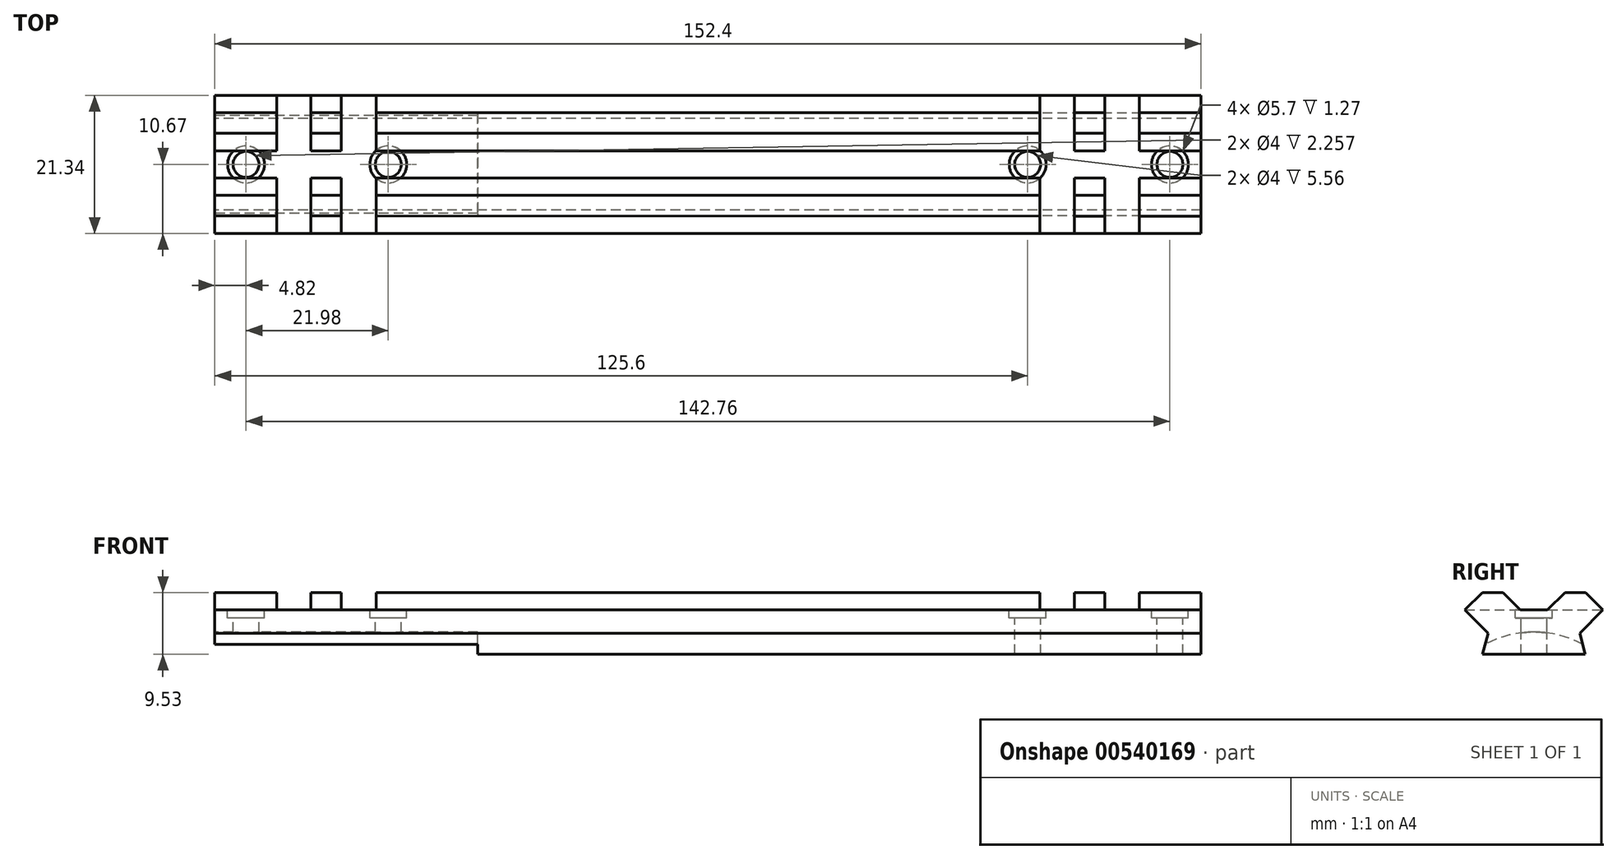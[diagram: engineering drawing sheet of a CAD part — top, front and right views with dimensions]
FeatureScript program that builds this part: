
annotation { "Feature Type Name" : "Feature", "Feature Type Description" : "" }
export const myFeature = defineFeature(function(context is Context, id is Id, definition is map)
    precondition{}
    {
        {
            var Q0;
            Q0=qCreatedBy(makeId("Front.planeOp"),FACE);
            var sketch = newSketch(context, id + "F0", { "sketchPlane" : qUnion([Q0])});
            skLineSegment(sketch, "E0", {"start": v(-76.2, 0) * mm, "end": v(76.2, 0) * mm});
            skLineSegment(sketch, "E1.0", {"start": v(-76.2, 9.53) * mm, "end": v(76.2, 9.52) * mm});
            skLineSegment(sketch, "E2", {"start": v(-76.2, 0) * mm, "end": v(-76.2, 9.53) * mm});
            skLineSegment(sketch, "E3", {"start": v(76.2, 0) * mm, "end": v(76.2, 9.52) * mm});
            skSolve(sketch);
        }
        {
            var Q0;
            Q0=makeQuery(id+"F0.imprint","IMPRINT",FACE,{"disambiguationData":[TD([[makeQuery(id+"F0.imprint","IMPRINT",EDGE,{"derivedFrom":sQuery(id+"F0.wireOp",EDGE,"E0")}),1.0]])]});
            extrude(context, id + "F1", {"entities" : qUnion([Q0]), "endBound" : BoundingType.SYMMETRIC, "depth" : 21.34 * mm, "offsetDistance" : 25.4 * mm});
        }
        {
            var Q0;
            Q0=makeQuery(id+"F1.opExtrude","SWEPT_FACE",FACE,{"disambiguationData":[OSD([sQuery(id+"F0.wireOp",EDGE,"E2")])]});
            var sketch = newSketch(context, id + "F2", { "sketchPlane" : qUnion([Q0])});
            skLineSegment(sketch, "E4", {"start": v(-10.67, 6.83) * mm, "end": v(-7.97, 9.53) * mm});
            skLineSegment(sketch, "E5", {"start": v(-10.67, 6.83) * mm, "end": v(-7.08, 3.24) * mm});
            skLineSegment(sketch, "E6", {"start": v(0, 0) * mm, "end": v(-7.94, 0) * mm});
            skLineSegment(sketch, "E7", {"start": v(-7.94, 0) * mm, "end": v(-7.08, 3.24) * mm});
            skLineSegment(sketch, "E8", {"start": v(0, 6.83) * mm, "end": v(-2.1, 6.83) * mm});
            skLineSegment(sketch, "E9", {"start": v(-2.1, 6.83) * mm, "end": v(-4.8, 9.53) * mm});
            skLineSegment(sketch, "E10", {"start": v(-4.8, 9.53) * mm, "end": v(-7.97, 9.53) * mm});
            skLineSegment(sketch, "E11.MirrorCS", {"start": v(0, 6.83) * mm, "end": v(2.1, 6.83) * mm});
            skLineSegment(sketch, "E12.MirrorCS", {"start": v(2.1, 6.83) * mm, "end": v(4.8, 9.53) * mm});
            skLineSegment(sketch, "E13.MirrorCS", {"start": v(4.8, 9.53) * mm, "end": v(7.97, 9.53) * mm});
            skLineSegment(sketch, "E14.MirrorCS", {"start": v(10.67, 6.83) * mm, "end": v(7.97, 9.53) * mm});
            skLineSegment(sketch, "E15.MirrorCS", {"start": v(10.67, 6.83) * mm, "end": v(7.08, 3.24) * mm});
            skLineSegment(sketch, "E16.MirrorCS", {"start": v(7.94, 0) * mm, "end": v(7.08, 3.24) * mm});
            skLineSegment(sketch, "E17.MirrorCS", {"start": v(0, 0) * mm, "end": v(7.94, 0) * mm});
            skSolve(sketch);
        }
        {
            var Q0;
            {var subQ0=sQuery(id+"F2.wireOp",EDGE,"E5");Q0=makeQuery(id+"F2.imprint","IMPRINT",FACE,{"disambiguationData":[TD([[makeQuery(id+"F2.imprint","IMPRINT",EDGE,{"derivedFrom":subQ0}),-1.0]])]});}
            var Q1;
            {var subQ0=sQuery(id+"F2.wireOp",EDGE,"E4");Q1=makeQuery(id+"F2.imprint","IMPRINT",FACE,{"disambiguationData":[TD([[makeQuery(id+"F2.imprint","IMPRINT",EDGE,{"derivedFrom":subQ0}),1.0]])]});}
            var Q2;
            Q2=makeQuery(id+"F2.imprint","IMPRINT",FACE,{"disambiguationData":[TD([[makeQuery(id+"F2.imprint","IMPRINT",EDGE,{"derivedFrom":sQuery(id+"F2.wireOp",EDGE,"E8")}),-1.0]])]});
            var Q3;
            {var subQ0=sQuery(id+"F2.wireOp",EDGE,"E14.MirrorCS");Q3=makeQuery(id+"F2.imprint","IMPRINT",FACE,{"disambiguationData":[TD([[makeQuery(id+"F2.imprint","IMPRINT",EDGE,{"derivedFrom":subQ0}),-1.0]])]});}
            var Q4;
            {var subQ0=sQuery(id+"F2.wireOp",EDGE,"E15.MirrorCS");Q4=makeQuery(id+"F2.imprint","IMPRINT",FACE,{"disambiguationData":[TD([[makeQuery(id+"F2.imprint","IMPRINT",EDGE,{"derivedFrom":subQ0}),1.0]])]});}
            extrude(context, id + "F3", {"entities" : qUnion([Q0, Q1, Q2, Q3, Q4]), "operationType" : NewBodyOperationType.REMOVE, "oppositeDirection" : true, "depth" : 152.4 * mm, "offsetDistance" : 25.4 * mm});
        }
        {
            var Q0;
            Q0=makeQuery(id+"F1.opExtrude","SWEPT_FACE",FACE,{"disambiguationData":[OSD([sQuery(id+"F0.wireOp",EDGE,"E2")])]});
            var sketch = newSketch(context, id + "F4", { "sketchPlane" : qUnion([Q0])});
            skCircle(sketch, "E18", {"center": v(0, -12.45) * mm, "radius": 15.88 * mm});
            skLineSegment(sketch, "E19", {"start": v(-9.85, 0) * mm, "end": v(9.85, 0) * mm});
            skSolve(sketch);
        }
        {
            var Q0;
            {var subQ0=sQuery(id+"F4.wireOp",EDGE,"E18");var subQ1=makeQuery(id+"F3.boolean.opBoolean","COPY",EDGE,{"derivedFrom":makeQuery(id+"F3.opExtrude","CAP_EDGE",EDGE,{"disambiguationData":[OSD([sQuery(id+"F2.wireOp",EDGE,"E16.MirrorCS")])],"isStart":true})});var subQ2=makeQuery(id+"F4.imprint","INTERSECT",VERTEX,{"derivedFrom":[subQ1,subQ0]});Q0=makeQuery(id+"F4.imprint","IMPRINT",FACE,{"disambiguationData":[TD([[makeQuery(id+"F4.imprint","IMPRINT",EDGE,{"disambiguationData":[TD([[subQ2,-1.0]])],"derivedFrom":subQ0}),1.0]])]});}
            extrude(context, id + "F5", {"entities" : qUnion([Q0]), "operationType" : NewBodyOperationType.REMOVE, "oppositeDirection" : true, "depth" : 40.64 * mm, "offsetDistance" : 25.4 * mm});
        }
        {
            var Q0;
            Q0=makeQuery(id+"F3.boolean.opBoolean","COPY",FACE,{"derivedFrom":makeQuery(id+"F3.opExtrude","SWEPT_FACE",FACE,{"disambiguationData":[OSD([sQuery(id+"F2.wireOp",EDGE,"E8"),sQuery(id+"F2.wireOp",EDGE,"E11.MirrorCS")])]})});
            var sketch = newSketch(context, id + "F6", { "sketchPlane" : qUnion([Q0])});
            skLineSegment(sketch, "E20", {"start": v(-66.67, -10.86) * mm, "end": v(-66.67, 11.03) * mm});
            skPoint(sketch, "E21.orphan", {"position": v(-66.67, 0) * mm});
            skLineSegment(sketch, "E22.0", {"start": v(-61.34, -10.86) * mm, "end": v(-61.34, 11.03) * mm});
            skLineSegment(sketch, "E23.0", {"start": v(-56.64, -10.86) * mm, "end": v(-56.64, 11.03) * mm});
            skLineSegment(sketch, "E24.0", {"start": v(-51.3, -10.86) * mm, "end": v(-51.3, 11.03) * mm});
            skLineSegment(sketch, "E25", {"start": v(-66.67, 11.03) * mm, "end": v(-61.34, 11.03) * mm});
            skLineSegment(sketch, "E26", {"start": v(-66.67, -10.86) * mm, "end": v(-61.34, -10.86) * mm});
            skCircle(sketch, "E27", {"center": v(-71.38, 0) * mm, "radius": 2.86 * mm});
            skCircle(sketch, "E28", {"center": v(-49.4, 0) * mm, "radius": 2.86 * mm});
            skCircle(sketch, "E29.MirrorC", {"center": v(49.4, 0) * mm, "radius": 2.86 * mm});
            skCircle(sketch, "E30.MirrorC", {"center": v(71.38, 0) * mm, "radius": 2.86 * mm});
            skLineSegment(sketch, "E31.MirrorCS", {"start": v(66.67, -10.86) * mm, "end": v(66.67, 11.03) * mm});
            skLineSegment(sketch, "E32.MirrorCS", {"start": v(61.34, -10.86) * mm, "end": v(61.34, 11.03) * mm});
            skLineSegment(sketch, "E33.MirrorCS", {"start": v(56.64, -10.86) * mm, "end": v(56.64, 11.03) * mm});
            skLineSegment(sketch, "E34.MirrorCS", {"start": v(51.3, -10.86) * mm, "end": v(51.3, 11.03) * mm});
            skLineSegment(sketch, "E35.MirrorCS", {"start": v(66.67, 11.03) * mm, "end": v(61.34, 11.03) * mm});
            skLineSegment(sketch, "E36.MirrorCS", {"start": v(66.67, -10.86) * mm, "end": v(61.34, -10.86) * mm});
            skLineSegment(sketch, "E37.trimOffspring", {"start": v(-56.64, 11.03) * mm, "end": v(-51.3, 11.03) * mm});
            skLineSegment(sketch, "E38.trimOffspring", {"start": v(-56.64, -10.86) * mm, "end": v(-51.3, -10.86) * mm});
            skLineSegment(sketch, "E39.trimOffspring", {"start": v(56.64, 11.03) * mm, "end": v(51.3, 11.03) * mm});
            skLineSegment(sketch, "E40.trimOffspring", {"start": v(56.64, -10.86) * mm, "end": v(51.3, -10.86) * mm});
            skSolve(sketch);
        }
        {
            var Q0;
            {var subQ0=sQuery(id+"F6.wireOp",EDGE,"E25");Q0=makeQuery(id+"F6.imprint","IMPRINT",FACE,{"disambiguationData":[TD([[makeQuery(id+"F6.imprint","IMPRINT",EDGE,{"derivedFrom":subQ0}),-1.0]])]});}
            var Q1;
            {var subQ0=sQuery(id+"F6.wireOp",EDGE,"E20");var subQ1=makeQuery(id+"F3.boolean.opBoolean","COPY",EDGE,{"derivedFrom":makeQuery(id+"F3.opExtrude","SWEPT_EDGE",EDGE,{"disambiguationData":[OSD([sQuery(id+"F2.wireOp",EDGE,"E11.MirrorCS"),sQuery(id+"F2.wireOp",EDGE,"E12.MirrorCS")])]})});var subQ2=makeQuery(id+"F6.imprint","INTERSECT",VERTEX,{"derivedFrom":[subQ1,subQ0]});Q1=makeQuery(id+"F6.imprint","IMPRINT",FACE,{"disambiguationData":[TD([[makeQuery(id+"F6.imprint","IMPRINT",EDGE,{"disambiguationData":[TD([[subQ2,-1.0]])],"derivedFrom":subQ0}),-1.0]])]});}
            var Q2;
            {var subQ0=sQuery(id+"F6.wireOp",EDGE,"E26");Q2=makeQuery(id+"F6.imprint","IMPRINT",FACE,{"disambiguationData":[TD([[makeQuery(id+"F6.imprint","IMPRINT",EDGE,{"derivedFrom":subQ0}),1.0]])]});}
            var Q3;
            {var subQ0=sQuery(id+"F6.wireOp",EDGE,"E38.trimOffspring");Q3=makeQuery(id+"F6.imprint","IMPRINT",FACE,{"disambiguationData":[TD([[makeQuery(id+"F6.imprint","IMPRINT",EDGE,{"derivedFrom":subQ0}),1.0]])]});}
            var Q4;
            {var subQ0=sQuery(id+"F6.wireOp",EDGE,"E28");var subQ1=sQuery(id+"F6.wireOp",EDGE,"E24.0");var subQ2=makeQuery(id+"F6.imprint","INTERSECT",VERTEX,{"disambiguationData":[OD(0.0)],"derivedFrom":[subQ1,subQ0]});Q4=makeQuery(id+"F6.imprint","IMPRINT",FACE,{"disambiguationData":[TD([[makeQuery(id+"F6.imprint","IMPRINT",EDGE,{"disambiguationData":[TD([[subQ2,1.0]])],"derivedFrom":subQ0}),-1.0]])]});}
            var Q5;
            {var subQ0=sQuery(id+"F6.wireOp",EDGE,"E37.trimOffspring");Q5=makeQuery(id+"F6.imprint","IMPRINT",FACE,{"disambiguationData":[TD([[makeQuery(id+"F6.imprint","IMPRINT",EDGE,{"derivedFrom":subQ0}),-1.0]])]});}
            var Q6;
            {var subQ0=sQuery(id+"F6.wireOp",EDGE,"E34.MirrorCS");var subQ1=sQuery(id+"F6.wireOp",EDGE,"E29.MirrorC");var subQ2=makeQuery(id+"F6.imprint","INTERSECT",VERTEX,{"disambiguationData":[OD(0.0)],"derivedFrom":[subQ1,subQ0]});Q6=makeQuery(id+"F6.imprint","IMPRINT",FACE,{"disambiguationData":[TD([[makeQuery(id+"F6.imprint","IMPRINT",EDGE,{"disambiguationData":[TD([[subQ2,1.0]])],"derivedFrom":subQ1}),1.0]])]});}
            var Q7;
            {var subQ0=sQuery(id+"F6.wireOp",EDGE,"E39.trimOffspring");Q7=makeQuery(id+"F6.imprint","IMPRINT",FACE,{"disambiguationData":[TD([[makeQuery(id+"F6.imprint","IMPRINT",EDGE,{"derivedFrom":subQ0}),1.0]])]});}
            var Q8;
            {var subQ0=sQuery(id+"F6.wireOp",EDGE,"E40.trimOffspring");Q8=makeQuery(id+"F6.imprint","IMPRINT",FACE,{"disambiguationData":[TD([[makeQuery(id+"F6.imprint","IMPRINT",EDGE,{"derivedFrom":subQ0}),-1.0]])]});}
            var Q9;
            {var subQ0=sQuery(id+"F6.wireOp",EDGE,"E36.MirrorCS");Q9=makeQuery(id+"F6.imprint","IMPRINT",FACE,{"disambiguationData":[TD([[makeQuery(id+"F6.imprint","IMPRINT",EDGE,{"derivedFrom":subQ0}),-1.0]])]});}
            var Q10;
            {var subQ0=sQuery(id+"F6.wireOp",EDGE,"E31.MirrorCS");var subQ1=makeQuery(id+"F3.boolean.opBoolean","COPY",EDGE,{"derivedFrom":makeQuery(id+"F3.opExtrude","SWEPT_EDGE",EDGE,{"disambiguationData":[OSD([sQuery(id+"F2.wireOp",EDGE,"E11.MirrorCS"),sQuery(id+"F2.wireOp",EDGE,"E12.MirrorCS")])]})});var subQ2=makeQuery(id+"F6.imprint","INTERSECT",VERTEX,{"derivedFrom":[subQ1,subQ0]});Q10=makeQuery(id+"F6.imprint","IMPRINT",FACE,{"disambiguationData":[TD([[makeQuery(id+"F6.imprint","IMPRINT",EDGE,{"disambiguationData":[TD([[subQ2,-1.0]])],"derivedFrom":subQ0}),1.0]])]});}
            var Q11;
            {var subQ0=sQuery(id+"F6.wireOp",EDGE,"E35.MirrorCS");Q11=makeQuery(id+"F6.imprint","IMPRINT",FACE,{"disambiguationData":[TD([[makeQuery(id+"F6.imprint","IMPRINT",EDGE,{"derivedFrom":subQ0}),1.0]])]});}
            extrude(context, id + "F7", {"entities" : qUnion([Q0, Q1, Q2, Q3, Q4, Q5, Q6, Q7, Q8, Q9, Q10, Q11]), "operationType" : NewBodyOperationType.REMOVE, "depth" : 25.4 * mm, "offsetDistance" : 25.4 * mm});
        }
        {
            var Q0;
            Q0=sQuery(id+"F6.wireOp",VERTEX,"E27.center");
            var Q1;
            Q1=sQuery(id+"F6.wireOp",VERTEX,"E30.MirrorC.center");
            var Q2;
            Q2=makeQuery(id+"F1.opExtrude","SWEPT_BODY",BODY,{"disambiguationData":[OSD([sQuery(id+"F0.wireOp",EDGE,"E0"),sQuery(id+"F0.wireOp",EDGE,"E1.0"),sQuery(id+"F0.wireOp",EDGE,"E2"),sQuery(id+"F0.wireOp",EDGE,"E3")])]});
            hole(context, id + "F8", {"style" : HoleStyle.C_BORE, "endStyle" : HoleEndStyle.THROUGH, "holeDiameter" : 4 * mm, "cBoreDiameter" : 5.7 * mm, "cBoreDepth" : 1.27 * mm, "isTappedThrough" : true, "tappedDepth" : 12.7 * mm, "tapClearance" : 3, "startFromSketch" : true, "locations" : qUnion([Q0, Q1]), "scope" : qUnion([Q2])});
        }
        {
            var Q0;
            Q0=sQuery(id+"F6.wireOp",VERTEX,"E28.center");
            var Q1;
            Q1=sQuery(id+"F6.wireOp",VERTEX,"E29.MirrorC.center");
            var Q2;
            Q2=makeQuery(id+"F1.opExtrude","SWEPT_BODY",BODY,{"disambiguationData":[OSD([sQuery(id+"F0.wireOp",EDGE,"E0"),sQuery(id+"F0.wireOp",EDGE,"E1.0"),sQuery(id+"F0.wireOp",EDGE,"E2"),sQuery(id+"F0.wireOp",EDGE,"E3")])]});
            hole(context, id + "F9", {"style" : HoleStyle.C_BORE, "endStyle" : HoleEndStyle.THROUGH, "holeDiameter" : 4 * mm, "cBoreDiameter" : 5.7 * mm, "cBoreDepth" : 1.27 * mm, "isTappedThrough" : true, "tappedDepth" : 12.7 * mm, "tapClearance" : 3, "startFromSketch" : true, "locations" : qUnion([Q0, Q1]), "scope" : qUnion([Q2])});
        }
    });
